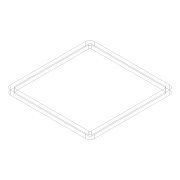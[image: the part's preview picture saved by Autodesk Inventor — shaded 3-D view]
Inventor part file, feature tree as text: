
AUTODESK INVENTOR PART (.ipt)
format: ipt  version: 2020 (Build 240168000, 168)  size: 116,736 bytes
history: native  units: mm
features: sketch x3, extrude x2, fillet x2
ambient origin geometry x8: Origin, YZ Plane, XZ Plane, XY Plane, X Axis, Y Axis, Z Axis, Center Point
bodies: Solid1 (feature_tree)
feature tree (7):
  extrude  "Extrusion1"  Depth=94.0mm
  extrude  "Extrusion2"  Depth=4.0mm
  fillet  "Fillet1"  Radius=4.0mm
  sketch  "Sketch3"  dims[d7=4.0mm d8=5.0mm d9=0.0mm d10=5.0mm d11=2.5mm d12=2.5mm d13=2.5mm d14=2.5mm d15=2.0mm]
  fillet  "Fillet2"  Radius=4.0mm
  sketch  "Sketch1"  dims[d0=94.0mm d1=94.0mm]
  sketch  "Sketch2"  dims[d2=5.0mm d3=0.0mm d4=4.0mm d5=4.0mm d6=4.0mm]
